# Revit family: P300189-020
name_source: partatom
category: Lighting Fixtures
revit_build: Autodesk Revit 2014 (Build: 20130308_1515(x64)
units: mm (PartAtom-declared; Revit-internal decimal feet)

## types (1)
- P300189-020
    Apparent Load = 60 VA
    Assembly Code = D5020200
    Color Filter = 16777215
    Connector Description = Lighting Connector
    Default Elevation = 48 "
    Description = Axle Collection One-Light Antique Bronze Vintage Style Bath Vanity Wall Light
    Dimming Lamp Color Temperature Shift = <None>
    Features = Mix old and new for charming character with the Axle Collection 1-Light Antique Bronze Vintage Bath Vanity Light. The round backplate is coated in an antique bronze finish accented by a golden satin brass vintage light base. The working gooseneck arm provides customizable tilt adjustment.
Application: Mix old and new for charming character with the Axle Collection 1-Light Antique Bronze Vintage Bath Vanity Light ideal for any entryway, hallway, foyer, bedroom, sitting room, living room, or bathroom.
Styles: Perfect for farmhouse, urban industrial, and vintage electric settings.
Finish: The round backplate is coated in an antique bronze finish accented by a golden satin brass vintage light base. The working gooseneck arm provides customizable tilt adjustment.
Materials: Constructed from steel to ensure a long product lifespan. Mount the light fixture facing up or down.
Glass: We recommend using vintage bulbs to enhance the wall light's timeless industrial aesthetic.
Bulbs: For ideal illumination, use 1 medium base bulb that is sold separately (60w max - LED/CFL/incandescent)
compatible with dimmable bulbs.
Dimensions: Measures 6-1/8-inch width by 6-3/4-inch height by 6-inch depth.
Certifications: uULus damp location listed.
Pairs With: Pairs with a variety of Progress Lighting fixtures.
Warranty: Our 1-Year Limited Warranty guarantees your complete satisfaction with your purchase and includes professional after-sales customer service support.
    Fixture distribution = Direct
    Glass = Paint - Hubbell - White Texture
    Gold = Hubbell - Gold
    Housing Material = Paint - Hubbell - Textured Camera Black
    Lamp = LED/CFL/incandescent
    Load Classification = Lighting
    Manufacturer = Progress Lighting
    Model = P300189-020
    Photometric Web File = generic
    Power Factor = 1
    Product Documentation Link = https://hubbellcdn.com
    Product Link = https://www.hubbell.com
    Tilt Angle = 60.00°
    URL = https://www.hubbell.com
    Voltage = 120 V
    Warranty = 1 year Warranty
    Wattage Comments = 60W
    Watts = 60 W

## geometry (parser evidence)
native form markers: Sweep x6
no freeform markers — native parametric forms only
